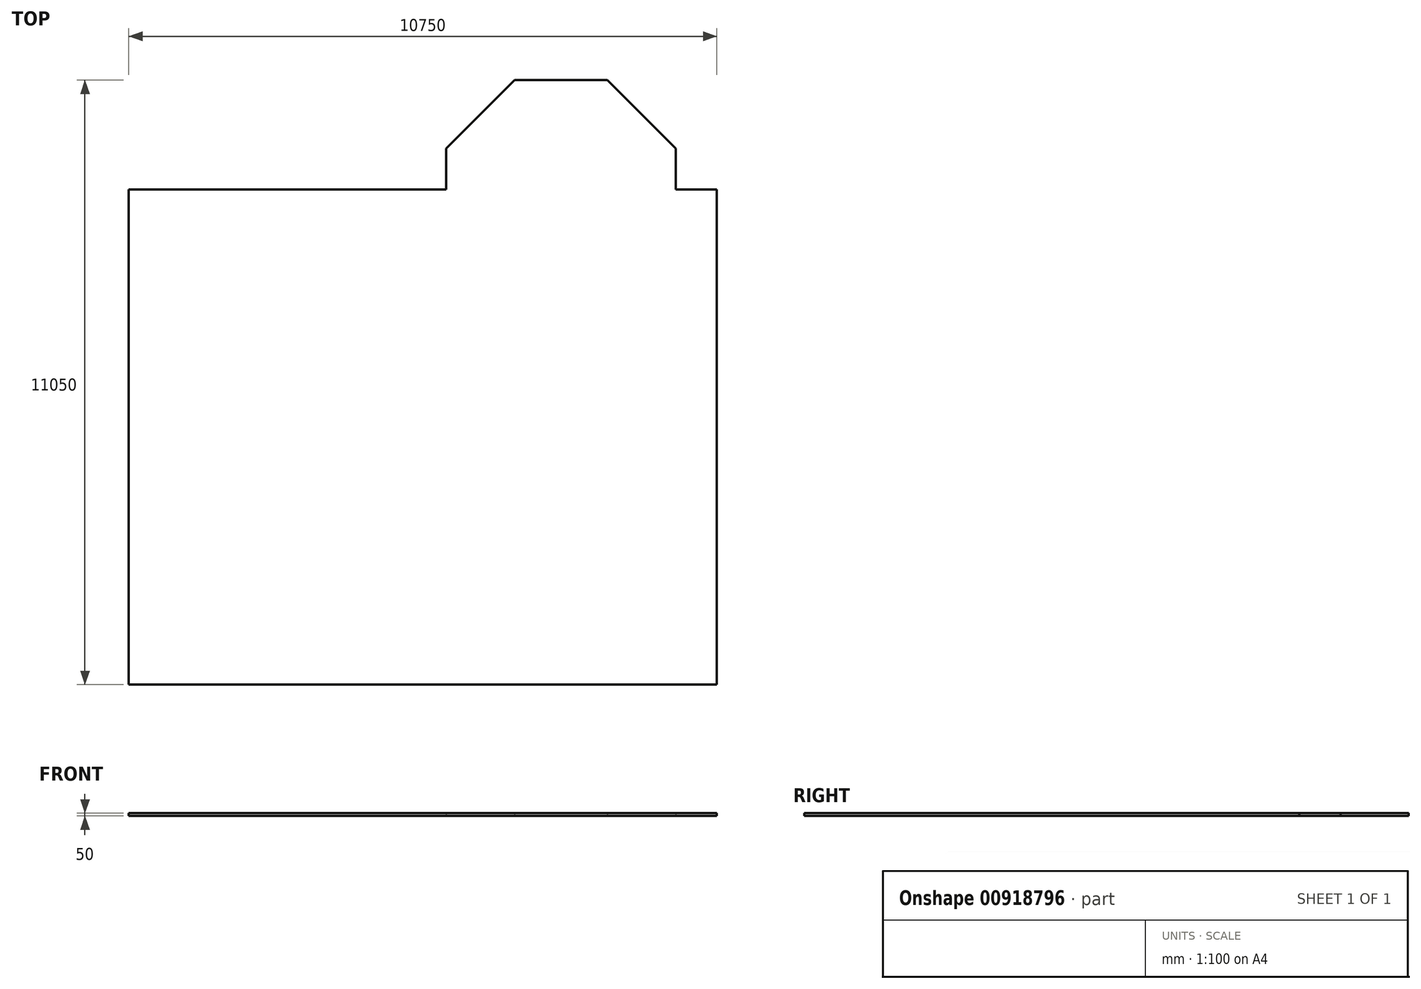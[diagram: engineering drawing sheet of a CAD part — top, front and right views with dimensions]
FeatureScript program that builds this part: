
annotation { "Feature Type Name" : "Feature", "Feature Type Description" : "" }
export const myFeature = defineFeature(function(context is Context, id is Id, definition is map)
    precondition{}
    {
        {
            var Q0;
            Q0=qCreatedBy(makeId("Top.planeOp"),FACE);
            var sketch = newSketch(context, id + "F0", { "sketchPlane" : qUnion([Q0])});
            skLineSegment(sketch, "E0.bottom", {"start": v(0, 0) * mm, "end": v(10750, 0) * mm});
            skLineSegment(sketch, "E0.top", {"start": v(0, 9050) * mm, "end": v(5800, 9050) * mm});
            skLineSegment(sketch, "E0.left", {"start": v(0, 0) * mm, "end": v(0, 9050) * mm});
            skLineSegment(sketch, "E0.right", {"start": v(10750, 0) * mm, "end": v(10750, 9050) * mm});
            skLineSegment(sketch, "E1", {"start": v(10000, 9050) * mm, "end": v(10000, 9800) * mm});
            skLineSegment(sketch, "E2", {"start": v(10000, 9800) * mm, "end": v(8750, 11050) * mm});
            skLineSegment(sketch, "E3", {"start": v(8750, 11050) * mm, "end": v(7050, 11050) * mm});
            skLineSegment(sketch, "E4", {"start": v(7050, 11050) * mm, "end": v(5800, 9800) * mm});
            skLineSegment(sketch, "E5", {"start": v(5800, 9800) * mm, "end": v(5800, 9050) * mm});
            skLineSegment(sketch, "E6.trimOffspring", {"start": v(10000, 9050) * mm, "end": v(10750, 9050) * mm});
            skSolve(sketch);
        }
        {
            var Q0;
            Q0=makeQuery(id+"F0.imprint","IMPRINT",FACE,{"disambiguationData":[TD([[makeQuery(id+"F0.imprint","IMPRINT",EDGE,{"derivedFrom":sQuery(id+"F0.wireOp",EDGE,"E0.bottom")}),1.0]])]});
            extrude(context, id + "F1", {"entities" : qUnion([Q0]), "depth" : 50 * mm, "offsetDistance" : 25 * mm});
        }
    });
